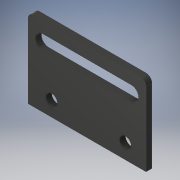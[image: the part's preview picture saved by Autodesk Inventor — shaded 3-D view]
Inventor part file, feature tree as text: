
AUTODESK INVENTOR PART (.ipt)
format: ipt  version: 2019 (Build 230136000, 136)  size: 119,296 bytes
history: native  units: mm
features: extrude x1, sketch x1
ambient origin geometry x8: Origin, YZ Plane, XZ Plane, XY Plane, X Axis, Y Axis, Z Axis, Center Point
bodies: Solid1 (feature_tree)
feature tree (2):
  extrude  "Extrusion1"  Depth=4.0mm
  sketch  "Sketch1"  dims[d0=40.0mm d1=4.0mm d2=4.0mm d3=25.0mm d4=8.0mm d5=2.0mm d6=5.0mm d7=15.0mm d8=5.0mm d9=2.0mm d10=0.0mm d11=25.0mm d12=4.0mm]
